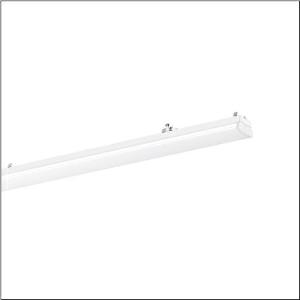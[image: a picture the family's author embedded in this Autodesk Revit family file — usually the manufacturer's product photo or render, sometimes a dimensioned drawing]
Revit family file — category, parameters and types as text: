
# Revit family: licross_r__11_recessed_opal_mo_51tl1d7n48xg_8506
name_source: partatom
category: Lighting Fixtures
units: mm (PartAtom-declared; Revit-internal decimal feet)

## family parameters
Cut with Voids When Loaded = No
Host = Face
Light Source = No
Part Type = Normal
Room Calculation Point = No
Round Connector Dimension = Use Diameter
Shared = No

## types (1)
- Licross® 11 recessed opal MO (1 x LED, 8490 lm, 48.5 W, 4000K)
    Apparent Load = 49 VA
    CIE Flux Codes = 44 73 91 87 100
    Color Rendering = 80
    Color Temperature = 4000K
    Default Elevation = 1800 mm
    Description = Licross® 11 recessed opal MO, luminaire insert, of sheet steel, coil coated, white, length: 1.500mm, width: 76mm, height: 87mm, LED rated luminous flux: 8.490lm, light colour: 840, control gear: ON/OFF, with plug, 3-pole, with phase selection, mains connection: 220..240V, AC, 50/60Hz, rated input power: 49W, halogen-free wiring, primary optical cover: cover, of PMMA, light emission: direct with ceiling illumination distribution, primary light characteristic: symmetric, protection rating (complete): IP40, insulation class (complete): insulation class I (protective earthing), certification: CE, ENEC, VDE, UKCA, protection symbol: D if used in an environment without relevant dust loads with corresponding accessories, impact resistance: IK06, permissible ambient temperature for indoor applications: -35..+35°C, corresponds to IFS (International Featured Standards) requirements for safety and quality in the food industry, reducing of maximum allowable ambient temperature of 5°C with ceiling mounting, packaging unit: 1 piece
    Height = 83 mm
    Lamp = 1 x LED
    Lamp Light Flux = 8490 lm
    Lamp Power = 48.5 W
    Lamp count = 1
    Length = 1500 mm
    Luminous efficacy = 175 lm/W
    Manufacturer = Siteco
    ModVariant = No
    Model = 51TL1D7N48XG
    Mounting Place = Ceiling
    Mounting Type = Pendant
    Number of Poles = 1
    OnlyDefault = Yes
    Power Factor = 1
    Product Name = Licross® 11 recessed opal MO
    Product group = luminaire insert
    ProductGroupID = 901
    Protection Class = Protection class I
    Protection Degree = IP 40
    RLX_Detail_Level = 1
    RLX_Emergency_Light_Flux = 0 lm
    RLX_Emergency_Type = 0
    RLX_Emergency_Type_DB = No
    RlxData = <blob elided: 23089 chars, md5=24251cd0>
    Socket = socket
    Standby Power = 0 W
    System Light Flux = 8490 lm
    System Power = 49 W
    Type Comments = Product without accessories
    Type Image = l_1313666.jpg
    URL = http://relux.com
    VarID = ---
    Voltage = 0 V
    Weight = 0.00 kg
    Width = 76 mm

## geometry (parser evidence)
native form markers: Blend x4, Sweep x13
no freeform markers — native parametric forms only
